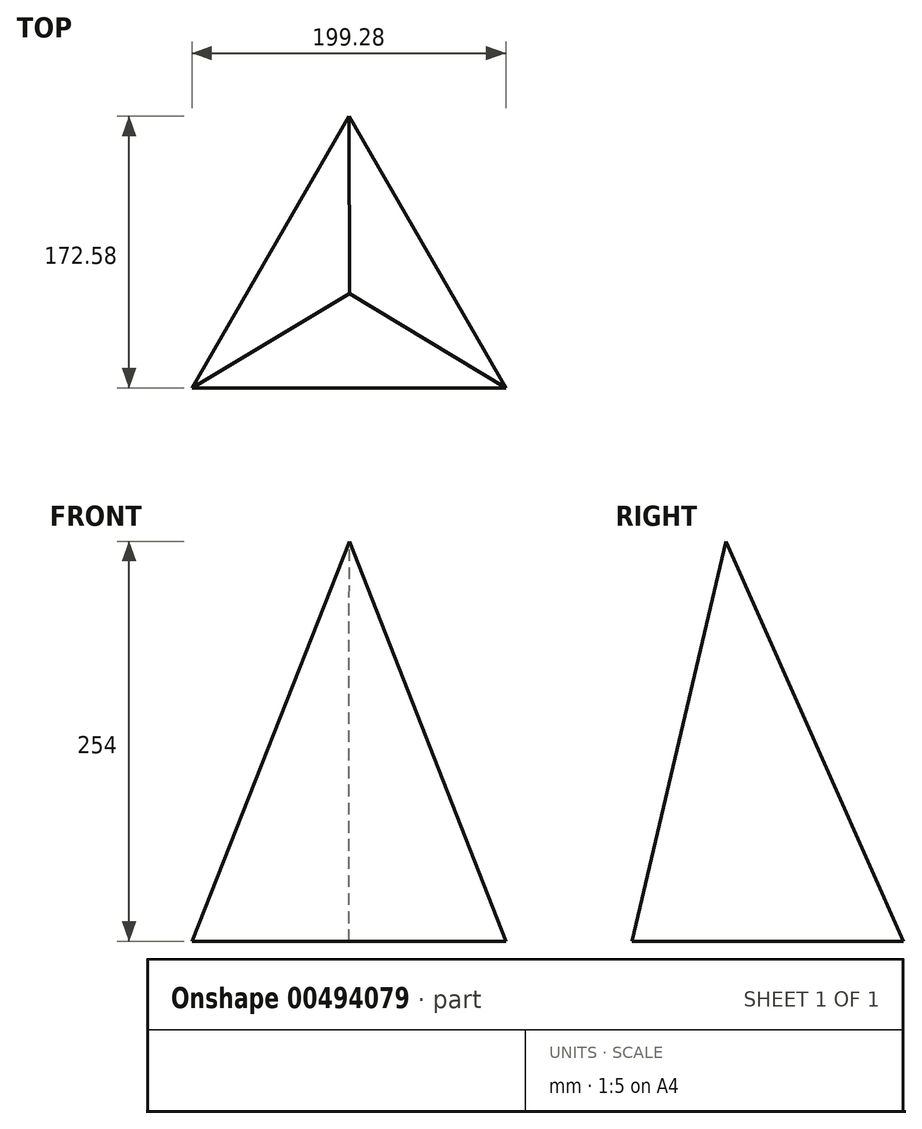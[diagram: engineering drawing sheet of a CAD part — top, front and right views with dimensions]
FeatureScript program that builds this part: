
annotation { "Feature Type Name" : "Feature", "Feature Type Description" : "" }
export const myFeature = defineFeature(function(context is Context, id is Id, definition is map)
    precondition{}
    {
        {
            var Q0;
            Q0=qCreatedBy(makeId("Top.planeOp"),FACE);
            var sketch = newSketch(context, id + "F0", { "sketchPlane" : qUnion([Q0])});
            skCircle(sketch, "E0.cCircle", {"center": v(0, 0) * mm, "radius": 115.05 * mm, "construction": true});
            skLineSegment(sketch, "E0.0", {"start": v(0, 115.05) * mm, "end": v(99.64, -57.53) * mm});
            skLineSegment(sketch, "E0.1", {"start": v(99.64, -57.53) * mm, "end": v(-99.64, -57.53) * mm});
            skLineSegment(sketch, "E0.2", {"start": v(-99.64, -57.53) * mm, "end": v(0, 115.05) * mm});
            skSolve(sketch);
        }
        {
            var Q0;
            Q0=qCreatedBy(makeId("Top.planeOp"),FACE);
            cPlane(context, id + "F1", {"entities" : qUnion([Q0]), "cplaneType" : CPlaneType.OFFSET, "offset" : 254 * mm, "width" : 152.4 * mm, "height" : 152.4 * mm});
        }
        {
            var Q0;
            Q0=qCreatedBy(id+"F1.planeOp",FACE);
            var sketch = newSketch(context, id + "F2", { "sketchPlane" : qUnion([Q0])});
            skPoint(sketch, "E1", {"position": v(0.3, 2.48) * mm});
            skSolve(sketch);
        }
        {
            var Q0;
            Q0=makeQuery(id+"F0.imprint","IMPRINT",FACE,{"disambiguationData":[TD([[makeQuery(id+"F0.imprint","IMPRINT",EDGE,{"derivedFrom":sQuery(id+"F0.wireOp",EDGE,"E0.0")}),-1.0]])]});
            var Q1;
            Q1=sQuery(id+"F2.wireOp",VERTEX,"E1");
            loft(context, id + "F3", {"sheetProfilesArray" : [{ "sheetProfileEntities" : qUnion([Q0]) }, { "sheetProfileEntities" : qUnion([Q1]) }]});
        }
    });
